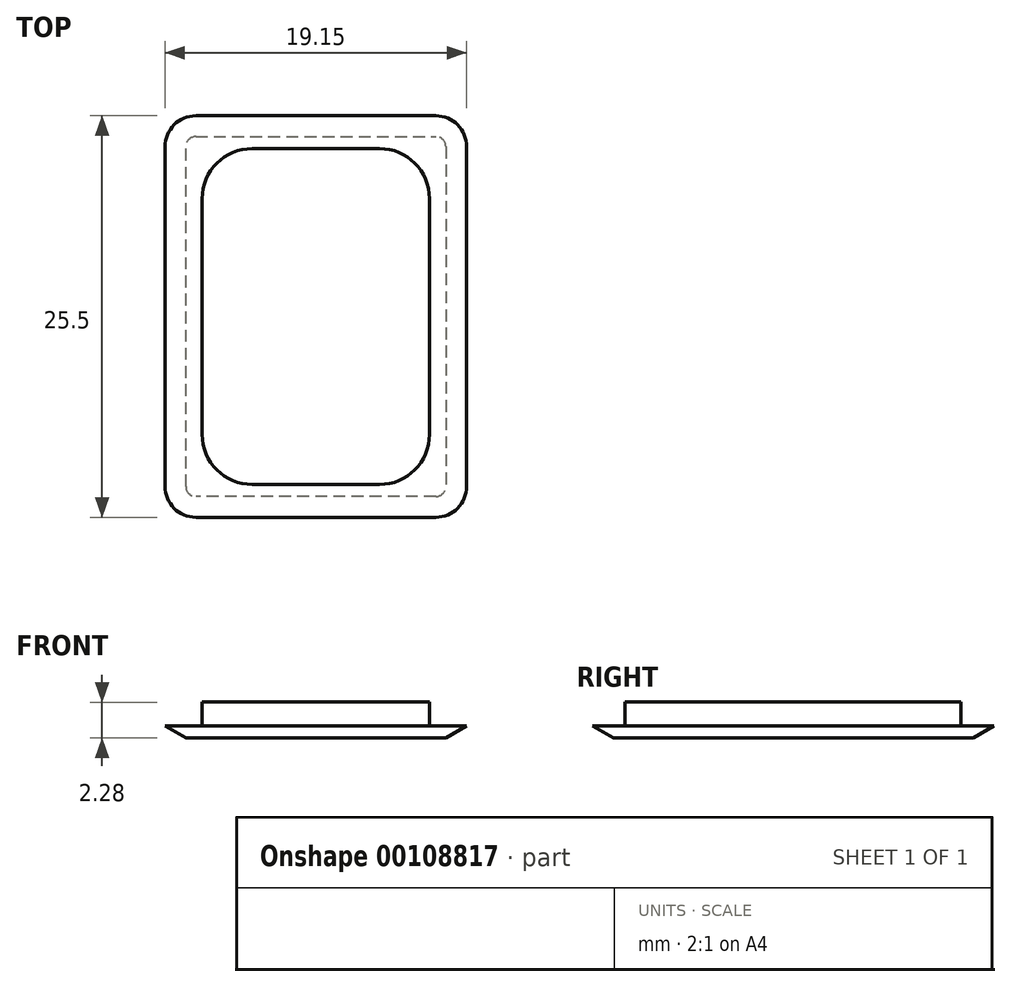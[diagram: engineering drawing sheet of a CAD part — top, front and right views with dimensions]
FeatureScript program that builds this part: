
annotation { "Feature Type Name" : "Feature", "Feature Type Description" : "" }
export const myFeature = defineFeature(function(context is Context, id is Id, definition is map)
    precondition{}
    {
        {
            var Q0;
            Q0=qCreatedBy(makeId("Top.planeOp"),FACE);
            var sketch = newSketch(context, id + "F0", { "sketchPlane" : qUnion([Q0])});
            skLineSegment(sketch, "E0.bottom", {"start": v(-45.48, 12.09) * mm, "end": v(-30.24, 12.09) * mm});
            skLineSegment(sketch, "E0.top", {"start": v(-45.48, 40.03) * mm, "end": v(-30.24, 40.03) * mm});
            skLineSegment(sketch, "E0.left", {"start": v(-48.66, 15.26) * mm, "end": v(-48.66, 36.85) * mm});
            skLineSegment(sketch, "E0.right", {"start": v(-27.07, 15.26) * mm, "end": v(-27.07, 36.85) * mm});
            skPoint(sketch, "E1.visualSharp", {"position": v(-48.66, 40.03) * mm});
            skArc(sketch, "E1.filletArc", {"start": v(-45.48, 40.03) * mm, "mid": v(-47.73, 39.1) * mm, "end": v(-48.66, 36.85) * mm});
            skPoint(sketch, "E2.visualSharp", {"position": v(-27.07, 40.03) * mm});
            skArc(sketch, "E2.filletArc", {"start": v(-27.07, 36.85) * mm, "mid": v(-28, 39.1) * mm, "end": v(-30.24, 40.03) * mm});
            skPoint(sketch, "E3.visualSharp", {"position": v(-48.66, 12.09) * mm});
            skArc(sketch, "E3.filletArc", {"start": v(-48.66, 15.26) * mm, "mid": v(-47.73, 13.02) * mm, "end": v(-45.48, 12.09) * mm});
            skPoint(sketch, "E4.visualSharp", {"position": v(-27.07, 12.09) * mm});
            skArc(sketch, "E4.filletArc", {"start": v(-30.24, 12.09) * mm, "mid": v(-28, 13.02) * mm, "end": v(-27.07, 15.26) * mm});
            skSolve(sketch);
        }
        {
            var Q0;
            Q0=makeQuery(id+"F0.imprint","IMPRINT",FACE,{"disambiguationData":[TD([[makeQuery(id+"F0.imprint","IMPRINT",EDGE,{"derivedFrom":sQuery(id+"F0.wireOp",EDGE,"E0.bottom")}),1.0]])]});
            var sketch = newSketch(context, id + "F1", { "sketchPlane" : qUnion([Q0])});
            skLineSegment(sketch, "E5.bottom", {"start": v(-41.9, 15.39) * mm, "end": v(-33.82, 15.39) * mm});
            skLineSegment(sketch, "E5.top", {"start": v(-41.9, 36.73) * mm, "end": v(-33.82, 36.73) * mm});
            skLineSegment(sketch, "E5.left", {"start": v(-45.07, 18.56) * mm, "end": v(-45.07, 33.55) * mm});
            skLineSegment(sketch, "E5.right", {"start": v(-30.65, 18.56) * mm, "end": v(-30.65, 33.55) * mm});
            skPoint(sketch, "E6.visualSharp", {"position": v(-45.07, 36.73) * mm});
            skArc(sketch, "E6.filletArc", {"start": v(-41.9, 36.73) * mm, "mid": v(-44.14, 35.8) * mm, "end": v(-45.07, 33.55) * mm});
            skPoint(sketch, "E7.visualSharp", {"position": v(-30.65, 36.73) * mm});
            skArc(sketch, "E7.filletArc", {"start": v(-30.65, 33.55) * mm, "mid": v(-31.58, 35.8) * mm, "end": v(-33.82, 36.73) * mm});
            skPoint(sketch, "E8.visualSharp", {"position": v(-30.65, 15.39) * mm});
            skArc(sketch, "E8.filletArc", {"start": v(-33.82, 15.39) * mm, "mid": v(-31.58, 16.32) * mm, "end": v(-30.65, 18.56) * mm});
            skPoint(sketch, "E9.visualSharp", {"position": v(-45.07, 15.39) * mm});
            skArc(sketch, "E9.filletArc", {"start": v(-45.07, 18.56) * mm, "mid": v(-44.14, 16.32) * mm, "end": v(-41.9, 15.39) * mm});
            skSolve(sketch);
        }
        {
            var Q0;
            Q0 = qSketchRegion(id + "F1", true);
            extrude(context, id + "F2", {"entities" : qUnion([Q0]), "depth" : 1.52 * mm});
        }
        {
            var Q0;
            Q0 = qSketchRegion(id + "F0", true);
            extrude(context, id + "F3", {"entities" : qUnion([Q0]), "operationType" : NewBodyOperationType.ADD, "oppositeDirection" : true, "depth" : 0.76 * mm});
        }
        {
            var Q0;
            Q0=makeQuery(id+"F3.opExtrude","CAP_EDGE",EDGE,{"disambiguationData":[OSD([sQuery(id+"F0.wireOp",EDGE,"E0.left")])],"isStart":false});
            var Q1;
            Q1=makeQuery(id+"F3.opExtrude","CAP_EDGE",EDGE,{"disambiguationData":[OSD([sQuery(id+"F0.wireOp",EDGE,"E0.top")])],"isStart":false});
            var Q2;
            Q2=makeQuery(id+"F3.opExtrude","CAP_EDGE",EDGE,{"disambiguationData":[OSD([sQuery(id+"F0.wireOp",EDGE,"E1.filletArc")])],"isStart":false});
            var Q3;
            Q3=makeQuery(id+"F3.opExtrude","CAP_EDGE",EDGE,{"disambiguationData":[OSD([sQuery(id+"F0.wireOp",EDGE,"E2.filletArc")])],"isStart":false});
            var Q4;
            Q4=makeQuery(id+"F3.opExtrude","CAP_EDGE",EDGE,{"disambiguationData":[OSD([sQuery(id+"F0.wireOp",EDGE,"E0.right")])],"isStart":false});
            var Q5;
            Q5=makeQuery(id+"F3.opExtrude","CAP_EDGE",EDGE,{"disambiguationData":[OSD([sQuery(id+"F0.wireOp",EDGE,"E4.filletArc")])],"isStart":false});
            var Q6;
            Q6=makeQuery(id+"F3.opExtrude","CAP_EDGE",EDGE,{"disambiguationData":[OSD([sQuery(id+"F0.wireOp",EDGE,"E0.bottom")])],"isStart":false});
            var Q7;
            Q7=makeQuery(id+"F3.opExtrude","CAP_EDGE",EDGE,{"disambiguationData":[OSD([sQuery(id+"F0.wireOp",EDGE,"E3.filletArc")])],"isStart":false});
            chamfer(context, id + "F4", {"entities" : qUnion([Q0, Q1, Q2, Q3, Q4, Q5, Q6, Q7]), "chamferType" : ChamferType.OFFSET_ANGLE, "width" : 2.54 * mm, "oppositeDirection" : false, "angle" : 30 * degree, "tangentPropagation" : true});
        }
    });
